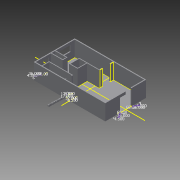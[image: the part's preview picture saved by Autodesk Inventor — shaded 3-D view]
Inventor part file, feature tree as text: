
AUTODESK INVENTOR PART (.ipt)
format: ipt  version: 2014 (Build 180170000, 170)  size: 565,248 bytes
history: native  units: in
note: dims shown in document units (in); Inventor stores cm internally (conversion verified against a paired STEP export)
features: extrude x21, sketch x17, projected_geometry x10, other x1
ambient origin geometry x8: Origin, YZ Plane, XZ Plane, XY Plane, X Axis, Y Axis, Z Axis, Center Point
bodies: Body1 (feature_tree)
feature tree (49):
  extrude  "Extrusion7"  Depth=5.0in
  extrude  "Extrusion8"  Depth=72.0in
  sketch  "Sketch5"  dims[d57=4.5in d58=60.0in d61=54.0in d64=432.0in]
  extrude  "Extrusion9"  Depth=54.0in
  extrude  "Extrusion10"  Depth=41.0in
  extrude  "Extrusion11"  Depth=93.0in
  extrude  "Extrusion12"  Depth=4.5in
  extrude  "Extrusion14"  Depth=73.0in
  extrude  "Extrusion16"  Depth=6.0in
  extrude  "Extrusion15"  Depth=73.0in
  extrude  "Extrusion17"  Depth=4.5in
  sketch  "Sketch13"  dims[d102=37.0in d103=73.0in]
  extrude  "Extrusion24"  Depth=4.5in
  extrude  "Extrusion26"  Depth=4.5in
  extrude  "Extrusion27"  Depth=48.0in
  other  "Open Doors"
  sketch  "Sketch23"  dims[d127=4.5in d128=252.0in d129=6.0in d130=46.0in d131=41.0in d132=4.5in d133=73.0in d134=93.0in d135=428.0in d136=97.0in d137=0.0in d138=1.0in d139=0.0in d140=80.0in d142=9.0in d143=32.0in d144=78.0in d145=28.0in d146=2.0in d147=2.0in d148=0.0in d149=1.0in d150=0.0in d151=16.0in d152=0.0in d153=66.0in d155=36.0in d156=43.0in d157=25.5in d158=16.0in d159=0.0in d192=35.0in d193=6.0in d195=35.0in d196=0.0in d197=7.25in d198=7.5in d199=7.25in d200=7.5in d201=7.25in d202=7.5in d203=7.25in d204=7.5in d205=7.25in d206=7.5in d207=7.25in d208=7.5in d209=7.25in d210=7.5in d211=7.25in d212=7.5in d213=7.25in d214=7.5in d215=7.25in d216=7.5in d217=7.25in d218=7.5in d219=7.25in d220=7.5in d221=7.25in d222=7.25in d223=7.5in d224=7.5in d225=7.5in d226=7.25in d227=35.0in d228=0.0in d230=1.0in d232=1.0in d233=0.0in d236=84.0in d237=20.25in d238=4.5in d240=0.001in d241=0.0in d252=17.0in d253=17.0in d256=8.5in d312=3.0in d313=0.0in d314=2.0in d315=0.0in d316=1.0in d317=0.0in d318=12.0in d319=17.0in d320=17.0in d321=8.5in d322=12.0in d323=17.0in d324=17.0in d325=8.5in d326=22.0in d327=22.0in d328=2.0in d329=0.0in d330=3.0in d331=0.0in d336=1.0in d337=0.0in d340=1.0in d341=0.0in d342=0.5in d343=0.0in d344=32.0in d346=4.5in d347=6.0in d348=36.0in d349=80.0in d350=0.0in d351=1.0in d352=0.0in d353=18.0in d355=1.0in d356=0.0in d357=24.0in d358=32.0in d360=4.5in d361=4.5in d362=36.0in d363=60.0deg d364=36.0in d365=4.5in d366=60.0deg d367=36.0in d368=4.5in d369=60.0deg]
  extrude  "Extrusion30"  Depth=240.0in
  extrude  "Extrusion28"  Depth=90.0in
  extrude  "Extrusion29"  Depth=4.5in
  extrude  "Extrusion18"  Depth=252.0in
  extrude  "Extrusion19"  Depth=6.0in
  extrude  "Extrusion20"  Depth=46.0in
  sketch  "Sketch15"  dims[d104=39.0in d105=4.5in]
  extrude  "Extrusion21"  Depth=41.0in
  extrude  "Extrusion22"  Depth=4.5in
  sketch  "Sketch1"  dims[d1=240.0in d4=5.0in d5=6.0in]
  sketch  "Sketch4"  dims[d14=72.0in d30=72.0in d40=432.0in]
  projected_geometry  "Projected Loop3"
  projected_geometry  "Projected Loop4"
  sketch  "Sketch6"  dims[d88=6.0in d89=41.0in d90=248.0in]
  projected_geometry  "Projected Loop5"
  projected_geometry  "Projected Loop6"
  sketch  "Sketch7"  dims[d91=37.0in d92=93.0in d93=117.0in]
  sketch  "Sketch9"  dims[d94=4.5in d95=4.5in]
  projected_geometry  "Projected Loop7"
  sketch  "Sketch11"  dims[d96=4.5in d97=73.0in]
  sketch  "Sketch12"  dims[d98=46.0in d99=36.0in d100=6.0in]
  projected_geometry  "Projected Loop8"
  sketch  "Sketch16"  dims[d106=4.5in d107=4.5in]
  projected_geometry  "Projected Loop13"
  projected_geometry  "Projected Loop14"
  projected_geometry  "Projected Loop15"
  sketch  "Sketch17"  dims[d108=4.5in d109=4.5in]
  sketch  "Sketch18"  dims[d110=263.0in d112=48.0in]
  sketch  "Sketch19"  dims[d117=45.5in d119=240.0in d120=6.0in]
  sketch  "Sketch20"  dims[d122=117.0in d123=90.0in]
  sketch  "Sketch21"  dims[d124=234.0in d125=4.5in]
  projected_geometry  "Projected Loop16"
